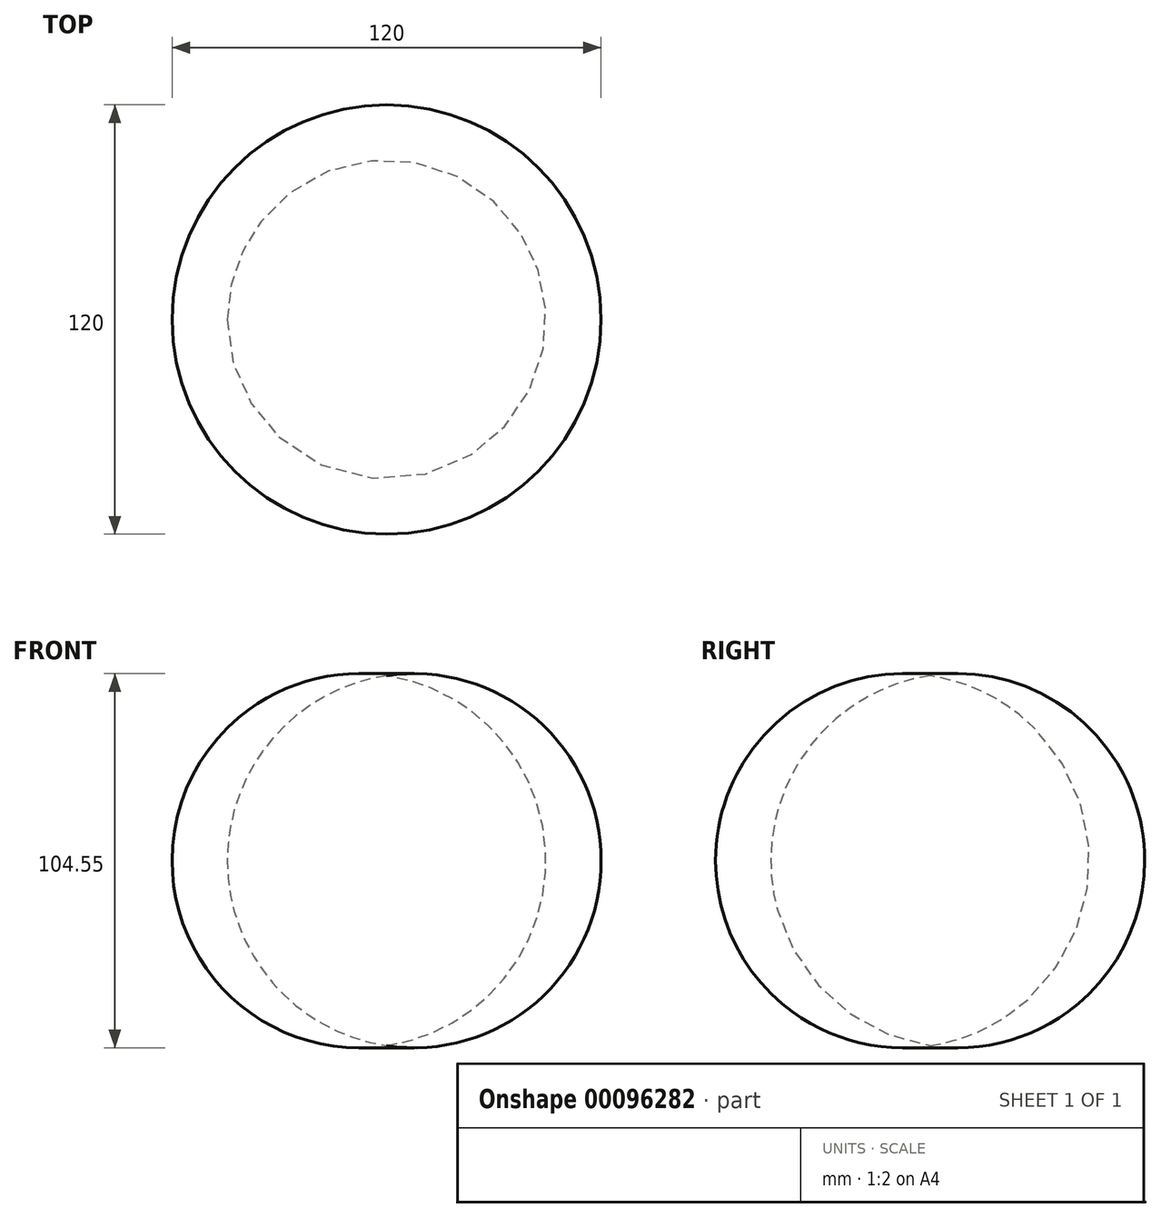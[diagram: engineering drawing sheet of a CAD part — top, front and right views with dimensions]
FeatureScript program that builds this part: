
annotation { "Feature Type Name" : "Feature", "Feature Type Description" : "" }
export const myFeature = defineFeature(function(context is Context, id is Id, definition is map)
    precondition{}
    {
        {
            var Q0;
            Q0=qCreatedBy(makeId("Front.planeOp"),FACE);
            var sketch = newSketch(context, id + "F0", { "sketchPlane" : qUnion([Q0])});
            skLineSegment(sketch, "E0", {"start": v(-49.76, 58.26) * mm, "end": v(-49.76, -45.15) * mm});
            skArc(sketch, "E1", {"start": v(-49.76, -45.15) * mm, "mid": v(-5.21, 6.56) * mm, "end": v(-49.76, 58.26) * mm});
            skSolve(sketch);
        }
        {
            var Q0;
            Q0=makeQuery(id+"F0.imprint","IMPRINT",FACE,{"disambiguationData":[TD([[makeQuery(id+"F0.imprint","IMPRINT",EDGE,{"derivedFrom":sQuery(id+"F0.wireOp",EDGE,"E0")}),1.0]])]});
            var Q1;
            Q1=sQuery(id+"F0.wireOp",EDGE,"E0");
            revolve(context, id + "F1", {"entities" : qUnion([Q0]), "axis" : qUnion([Q1]), "revolveType" : RevolveType.FULL});
        }
    });
